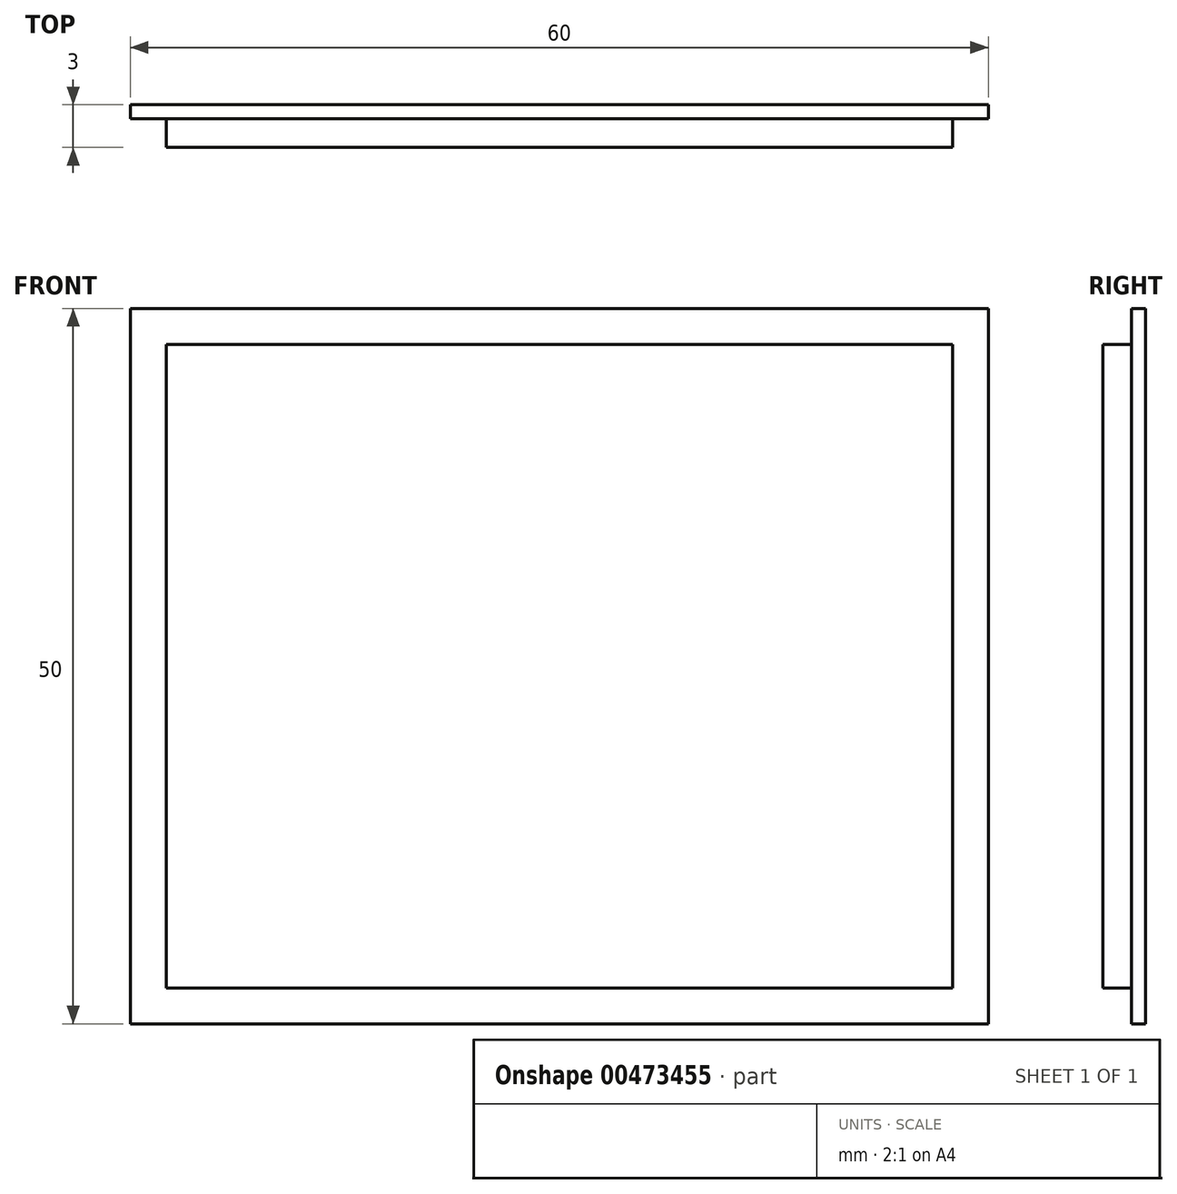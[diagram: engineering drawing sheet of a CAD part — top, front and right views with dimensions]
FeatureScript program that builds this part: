
annotation { "Feature Type Name" : "Feature", "Feature Type Description" : "" }
export const myFeature = defineFeature(function(context is Context, id is Id, definition is map)
    precondition{}
    {
        {
            var Q0;
            Q0=qCreatedBy(makeId("Front.planeOp"),FACE);
            var sketch = newSketch(context, id + "F0", { "sketchPlane" : qUnion([Q0])});
            skLineSegment(sketch, "E0.bottom", {"start": v(30, -25) * mm, "end": v(-30, -25) * mm});
            skLineSegment(sketch, "E0.top", {"start": v(30, 25) * mm, "end": v(-30, 25) * mm});
            skLineSegment(sketch, "E0.left", {"start": v(30, -25) * mm, "end": v(30, 25) * mm});
            skLineSegment(sketch, "E0.right", {"start": v(-30, -25) * mm, "end": v(-30, 25) * mm});
            skPoint(sketch, "E0.middle", {"position": v(0, 0) * mm});
            skSolve(sketch);
        }
        {
            var Q0;
            Q0=makeQuery(id+"F0.imprint","IMPRINT",FACE,{"disambiguationData":[TD([[makeQuery(id+"F0.imprint","IMPRINT",EDGE,{"derivedFrom":sQuery(id+"F0.wireOp",EDGE,"E0.bottom")}),-1.0]])]});
            var sketch = newSketch(context, id + "F1", { "sketchPlane" : qUnion([Q0])});
            skLineSegment(sketch, "E1.bottom", {"start": v(-27.5, -22.5) * mm, "end": v(27.5, -22.5) * mm});
            skLineSegment(sketch, "E1.top", {"start": v(-27.5, 22.5) * mm, "end": v(27.5, 22.5) * mm});
            skLineSegment(sketch, "E1.left", {"start": v(-27.5, -22.5) * mm, "end": v(-27.5, 22.5) * mm});
            skLineSegment(sketch, "E1.right", {"start": v(27.5, -22.5) * mm, "end": v(27.5, 22.5) * mm});
            skPoint(sketch, "E1.middle", {"position": v(0, 0) * mm});
            skSolve(sketch);
        }
        {
            var Q0;
            Q0 = qSketchRegion(id + "F1", true);
            extrude(context, id + "F2", {"entities" : qUnion([Q0]), "depth" : 3 * mm, "offsetDistance" : 25 * mm});
        }
        {
            var Q0;
            Q0=makeQuery(id+"F0.imprint","IMPRINT",FACE,{"disambiguationData":[TD([[makeQuery(id+"F0.imprint","IMPRINT",EDGE,{"derivedFrom":sQuery(id+"F0.wireOp",EDGE,"E0.bottom")}),-1.0]])]});
            extrude(context, id + "F3", {"entities" : qUnion([Q0]), "operationType" : NewBodyOperationType.ADD, "depth" : 1 * mm, "offsetDistance" : 25 * mm});
        }
    });
